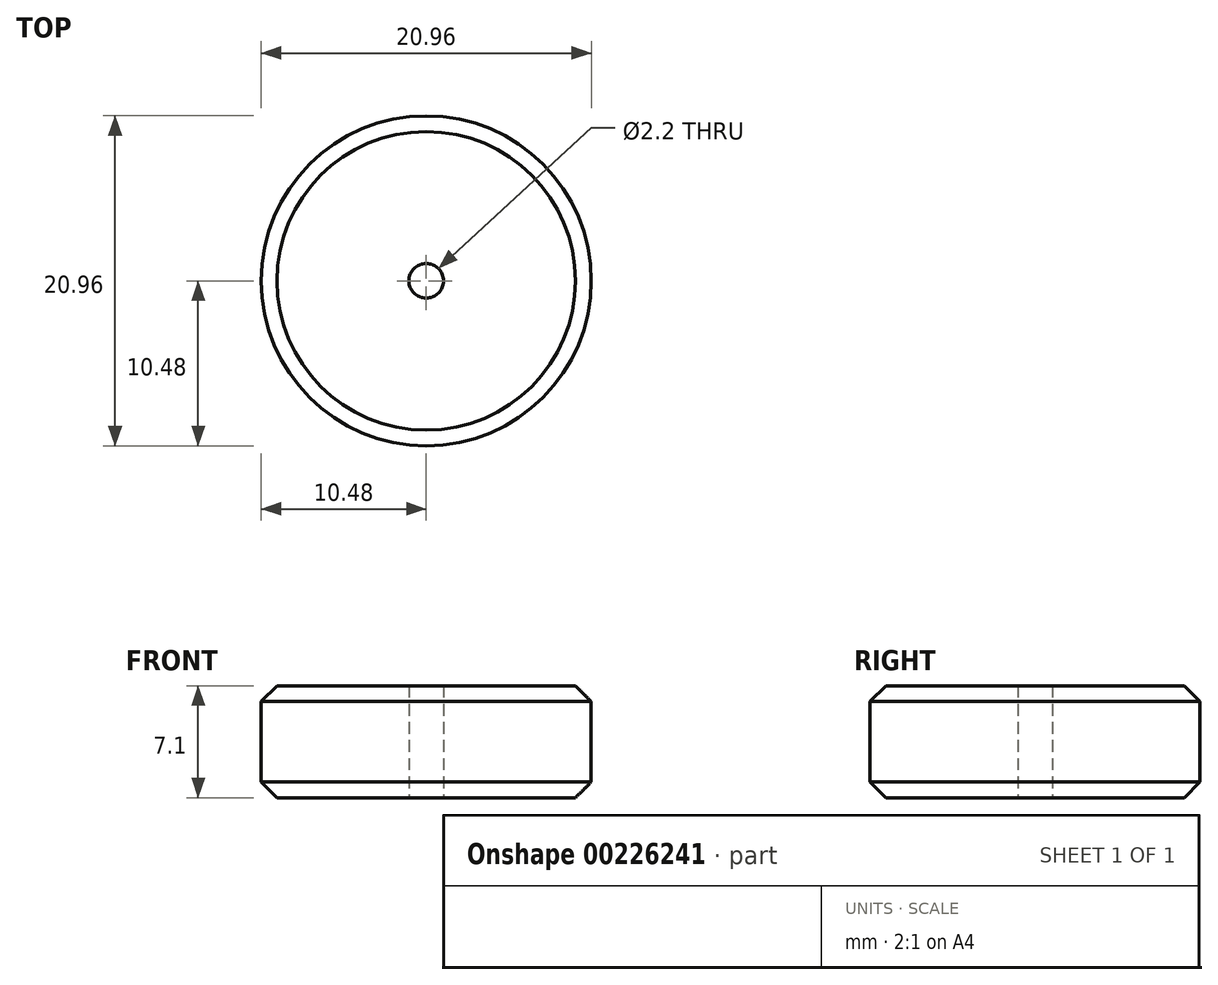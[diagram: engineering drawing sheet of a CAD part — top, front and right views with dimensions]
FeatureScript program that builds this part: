
annotation { "Feature Type Name" : "Feature", "Feature Type Description" : "" }
export const myFeature = defineFeature(function(context is Context, id is Id, definition is map)
    precondition{}
    {
        {
            var Q0;
            Q0=qCreatedBy(makeId("Top.planeOp"),FACE);
            var sketch = newSketch(context, id + "F0", { "sketchPlane" : qUnion([Q0])});
            skCircle(sketch, "E0", {"center": v(0, 0) * mm, "radius": 10.48 * mm});
            skCircle(sketch, "E1", {"center": v(0, 0) * mm, "radius": 1.1 * mm});
            skSolve(sketch);
        }
        {
            var Q0;
            Q0=qSketchRegion(id+"F0",true);
            extrude(context, id + "F1", {"entities" : qUnion([Q0]), "depth" : 341 / 48 * mm});
        }
        {
            var Q0;
            Q0=makeQuery(id+"F1.opExtrude","CAP_EDGE",EDGE,{"disambiguationData":[OSD([sQuery(id+"F0.wireOp",EDGE,"E0")])],"isStart":true});
            var Q1;
            Q1=makeQuery(id+"F1.opExtrude","CAP_EDGE",EDGE,{"disambiguationData":[OSD([sQuery(id+"F0.wireOp",EDGE,"E0")])],"isStart":false});
            chamfer(context, id + "F2", {"entities" : qUnion([Q0, Q1]), "width" : 1 * mm, "tangentPropagation" : true});
        }
    });
